# Revit family: 2321801 - ISSY Z8 VANITY 4 DRAW RIGHT EXT TOP 1500
name_source: partatom
category: Plumbing Fixtures
revit_build: Autodesk Revit 2015 (Build: 20140606_1530(x64)
units: mm (PartAtom-declared; Revit-internal decimal feet)

## types (2) — shared parameters
BIMobject category = Sanitary
Depth = 350
Description = Single floorstanding WC with dual outlet
Design country = Spain
Eco green certification = No
Edition number = 0
Flush Water Connection = 55 mm  [stored 0.180446 ft]
Flushing system = Washdown
Height = 440 mm  [stored 1.44357 ft]
IFC Classification = Furniture
Installation type = Floorstanding
Length = 350 mm
Manufacturer country = Spain
Manufacturer name = Roca
Manufacturer url = www.roca.com
Nominal height = 440
Nominal width = 540
Outlet type = Dual (vario)
Product SKU = 347477xx0
Product data url = http://roca.bimobject.com
Product family = The Gap
Product group = Toilets
QR code = http://roca.bimobject.com
Ref. No. = 347477000
Shape = Square
Suitable for Children = No
Suitable for Handicapped = No
Technical description = http://www.roca.com
UNSPSC Code = 301815
URL = http://roca.bimobject.com
Uniclass 1.4 Code = L7216
Uniclass 1.4 Description = Toilets
Uniclass 2.0 Code = SS-35-65-90
Uniclass 2.0 Description = Toilet Systems
Waste Water Connection = 102 mm
Weight Net (Kg) = 0
Width = 540 mm  [stored 1.77165 ft]

## type names (no varying parameters)
- White - The Gap - Roca
- Pergamon - The Gap - Roca

note: column(s) folded — value = type name in every type: Material

note: [stored X ft] marks values corroborated as IEEE doubles in the binary element streams (Revit-internal decimal feet)

## geometry (parser evidence)
native form markers: Sweep x3
no freeform markers — native parametric forms only
